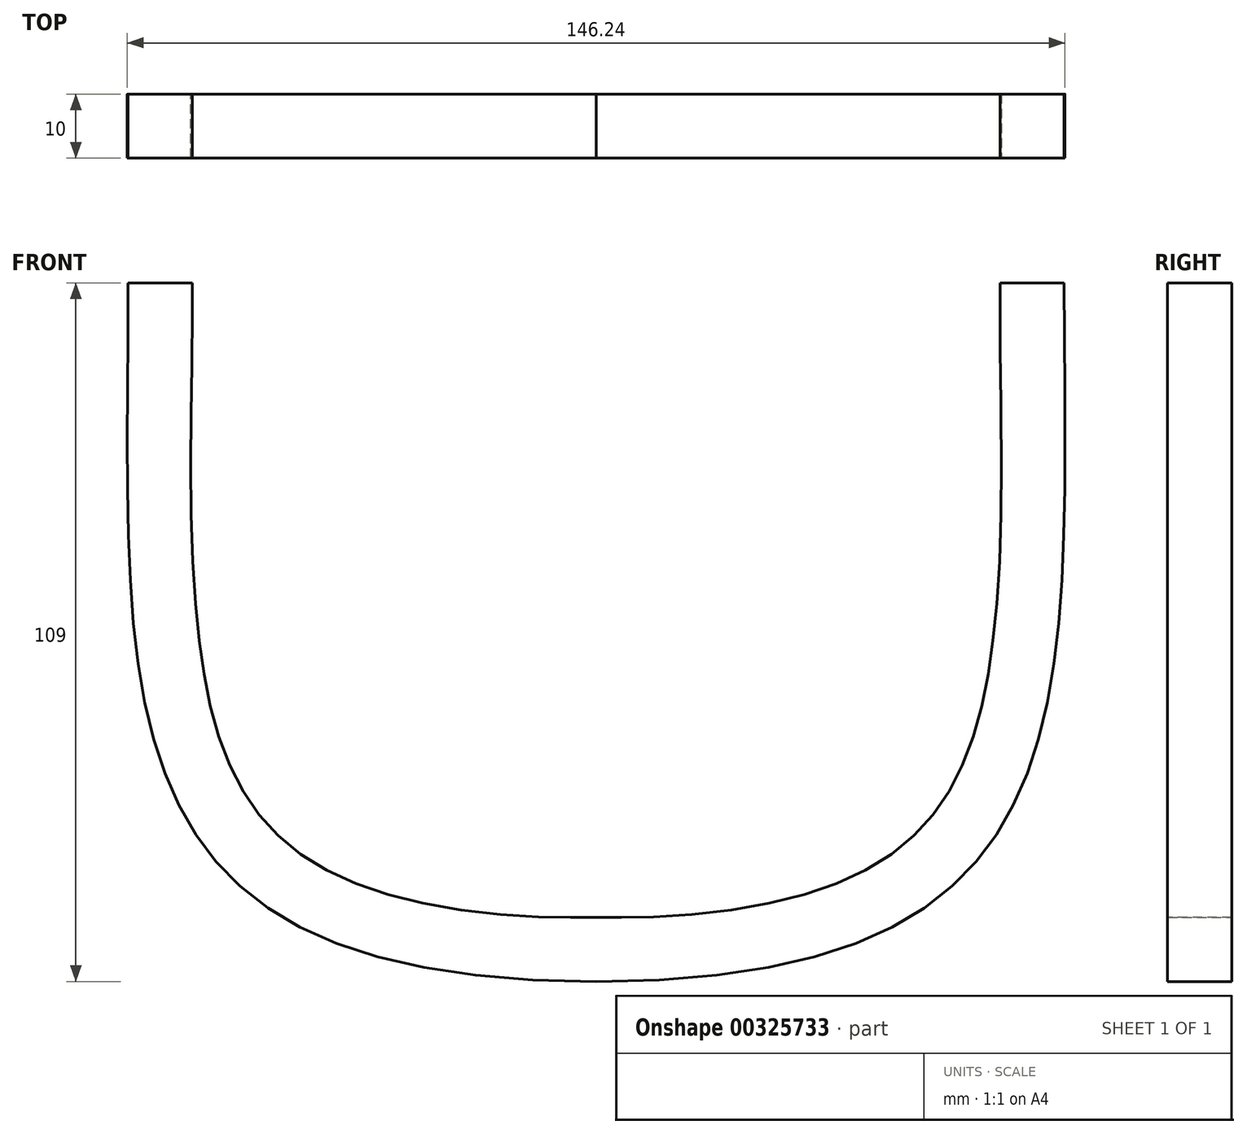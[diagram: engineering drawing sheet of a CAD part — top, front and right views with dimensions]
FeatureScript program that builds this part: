
annotation { "Feature Type Name" : "Feature", "Feature Type Description" : "" }
export const myFeature = defineFeature(function(context is Context, id is Id, definition is map)
    precondition{}
    {
        {
            var Q0;
            Q0=qCreatedBy(makeId("Front.planeOp"),FACE);
            var sketch = newSketch(context, id + "F0", { "sketchPlane" : qUnion([Q0])});
            skLineSegment(sketch, "E0", {"start": v(-73, 0) * mm, "end": v(73, 0) * mm, "construction": true});
            skLineSegment(sketch, "E1", {"start": v(73, 0) * mm, "end": v(73, 109) * mm, "construction": true});
            skLineSegment(sketch, "E2", {"start": v(0, 0) * mm, "end": v(0, 112.71) * mm, "construction": true});
            skFitSpline(sketch, "E3", {"points": [v(0, 0) * mm, v(73, 109) * mm], "startDerivative": vector(237.79, 0) * mm, "endDerivative": vector(0, 196.3) * mm});
            skFitSpline(sketch, "E4.MirrorCS", {"points": [v(0, 0) * mm, v(-73, 109) * mm], "startDerivative": vector(-237.79, 0) * mm, "endDerivative": vector(0, 196.3) * mm});
            skFitSpline(sketch, "E5.0", {"points": [v(0, 10) * mm, v(-4.72, 10) * mm, v(-13.45, 10.33) * mm, v(-24.47, 11.71) * mm, v(-33.52, 13.9) * mm, v(-40.76, 16.74) * mm, v(-46.4, 20.13) * mm, v(-50.82, 24) * mm, v(-54.33, 28.5) * mm, v(-57.16, 33.8) * mm, v(-59.4, 40.08) * mm, v(-61.05, 47.35) * mm, v(-62.16, 55.59) * mm, v(-63.03, 67.76) * mm, v(-63.2, 85.04) * mm, v(-63, 100.74) * mm, v(-63, 109) * mm]});
            skFitSpline(sketch, "E6.0", {"points": [v(0, 10) * mm, v(4.72, 10) * mm, v(13.45, 10.33) * mm, v(24.47, 11.71) * mm, v(33.52, 13.9) * mm, v(40.76, 16.74) * mm, v(46.4, 20.13) * mm, v(50.82, 24) * mm, v(54.33, 28.5) * mm, v(57.16, 33.8) * mm, v(59.4, 40.08) * mm, v(61.05, 47.35) * mm, v(62.16, 55.59) * mm, v(63.03, 67.76) * mm, v(63.2, 85.04) * mm, v(63, 100.74) * mm, v(63, 109) * mm]});
            skLineSegment(sketch, "E7", {"start": v(-63, 109) * mm, "end": v(-73, 109) * mm});
            skLineSegment(sketch, "E8", {"start": v(63, 109) * mm, "end": v(73, 109) * mm});
            skPoint(sketch, "E9", {"position": v(-63, 106.13) * mm});
            skPoint(sketch, "E10", {"position": v(63, 106.13) * mm});
            skPoint(sketch, "E11", {"position": v(-63.06, 96.13) * mm});
            skPoint(sketch, "E12", {"position": v(63.06, 96.13) * mm});
            skPoint(sketch, "E13", {"position": v(-63.12, 82.63) * mm});
            skPoint(sketch, "E14", {"position": v(63.12, 82.63) * mm});
            skPoint(sketch, "E15", {"position": v(-44.85, 96.41) * mm});
            skPoint(sketch, "E16", {"position": v(44.85, 96.13) * mm});
            skLineSegment(sketch, "E17", {"start": v(44.85, 96.13) * mm, "end": v(63.06, 96.13) * mm});
            skLineSegment(sketch, "E18", {"start": v(63.12, 82.63) * mm, "end": v(44.85, 96.13) * mm});
            skLineSegment(sketch, "E19", {"start": v(-44.85, 96.41) * mm, "end": v(-63.06, 96.13) * mm});
            skLineSegment(sketch, "E20", {"start": v(-63.12, 82.63) * mm, "end": v(-44.85, 96.41) * mm});
            skSolve(sketch);
        }
        {
            var Q0;
            Q0 = qSketchRegion(id + "F0", true);
            extrude(context, id + "F1", {"entities" : qUnion([Q0]), "endBound" : BoundingType.SYMMETRIC, "depth" : 10 * mm});
        }
    });
